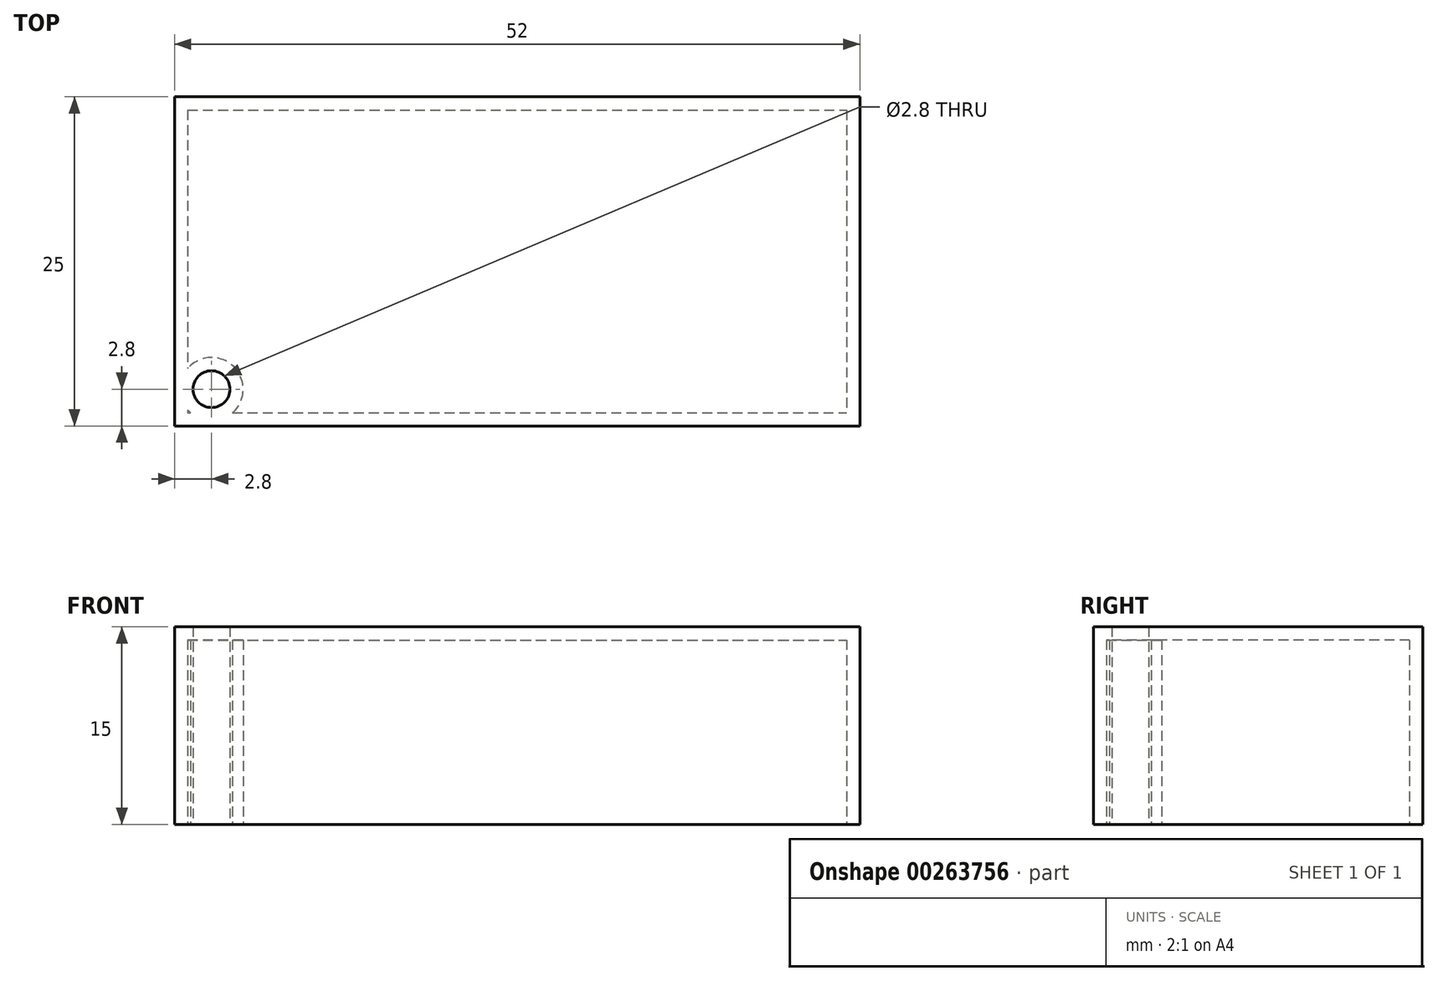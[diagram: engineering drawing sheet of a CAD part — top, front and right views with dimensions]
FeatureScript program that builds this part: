
annotation { "Feature Type Name" : "Feature", "Feature Type Description" : "" }
export const myFeature = defineFeature(function(context is Context, id is Id, definition is map)
    precondition{}
    {
        {
            var Q0;
            Q0=qCreatedBy(makeId("Top.planeOp"),FACE);
            var sketch = newSketch(context, id + "F0", { "sketchPlane" : qUnion([Q0])});
            skLineSegment(sketch, "E0.bottom", {"start": v(0, 0) * mm, "end": v(52, 0) * mm});
            skLineSegment(sketch, "E0.top", {"start": v(0, -25) * mm, "end": v(52, -25) * mm});
            skLineSegment(sketch, "E0.left", {"start": v(0, 0) * mm, "end": v(0, -25) * mm});
            skLineSegment(sketch, "E0.right", {"start": v(52, 0) * mm, "end": v(52, -25) * mm});
            skCircle(sketch, "E1", {"center": v(2.8, -22.2) * mm, "radius": 1.4 * mm});
            skSolve(sketch);
        }
        {
            var Q0;
            Q0=makeQuery(id+"F0.imprint","IMPRINT",FACE,{"disambiguationData":[TD([[makeQuery(id+"F0.imprint","IMPRINT",EDGE,{"derivedFrom":sQuery(id+"F0.wireOp",EDGE,"E0.bottom")}),-1.0]])]});
            var Q1;
            Q1=sQuery(id+"F0.wireOp",EDGE,"E0.right");
            var Q2;
            Q2=sQuery(id+"F0.wireOp",EDGE,"E0.top");
            var Q3;
            Q3=sQuery(id+"F0.wireOp",EDGE,"E0.bottom");
            var Q4;
            Q4=sQuery(id+"F0.wireOp",EDGE,"E0.left");
            extrude(context, id + "F1", {"entities" : qUnion([Q0]), "surfaceEntities" : qUnion([Q1, Q2, Q3, Q4]), "depth" : 15 * mm});
        }
        {
            var Q0;
            Q0=makeQuery(id+"F1.opExtrude","CAP_FACE",FACE,{"disambiguationData":[OSD([sQuery(id+"F0.wireOp",EDGE,"E0.bottom"),sQuery(id+"F0.wireOp",EDGE,"E0.top"),sQuery(id+"F0.wireOp",EDGE,"E0.left"),sQuery(id+"F0.wireOp",EDGE,"E0.right")])],"isStart":true});
            shell(context, id + "F2", {"entities" : qUnion([Q0]), "thickness" : 1 * mm});
        }
    });
